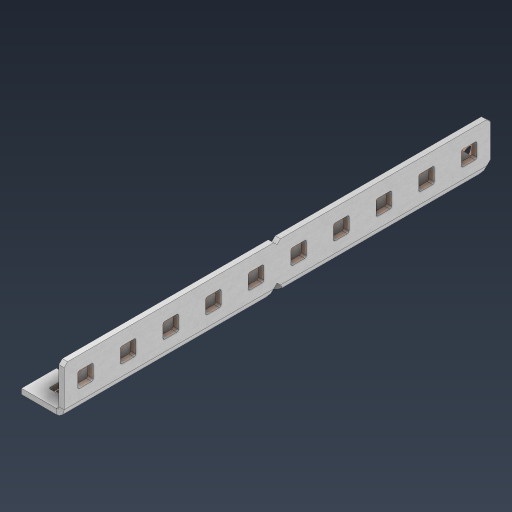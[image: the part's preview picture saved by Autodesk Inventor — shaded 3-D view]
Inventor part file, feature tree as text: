
AUTODESK INVENTOR PART (.ipt)
format: ipt  version: 2024.3 (Build 283343000, 343)  size: 601,600 bytes
history: native  units: in
note: dims shown in document units (in); Inventor stores cm internally (conversion verified against a paired STEP export)
features: other x37, extrude x28, sheet_metal_op x11, pattern_linear x2, mirror x1, chamfer x1, sketch x1
ambient origin geometry x8: Origin, YZ Plane, XZ Plane, XY Plane, X Axis, Y Axis, Z Axis, Center Point
bodies: Solid1 (feature_tree), Body (feature_tree)
feature tree (81):
  sheet_metal_op  "Flanges"
  other  "Flange Pattern Plane"
  other  "Flange Pattern Sketch"
  sheet_metal_op  "Flange Pattern"
  sheet_metal_op  "Body Pattern"
  pattern_linear  "Center Pattern"  Spacing1=5.0in  [1 undecoded]
  other  "Arc Length"
  mirror  "Notch Mirror"
  pattern_linear  "Notch Pattern"  Spacing1=0.0625in  [1 undecoded]
  chamfer  "End Chamfer"
  extrude  "Half Cut"  Depth=0.0625in
  other  "Plate1"
  sketch  "Sketch2"  dims[d0=1.0in d1=5.0in d2=0.0625in d3=0.0625in d4=0.0312in d5=0.125in d6=0.0625in d7=0.5in d8=90.0deg d9=0.0312in d10=0.25in d11=0.0625in d12=0.0625in d16=0.182in d17=0.02in d18=0.0625in d19=0.0in d20=0.25in d21=0.25in d38=3.937in d40=0.5in d41=0.3937in d43=1.0in d46=0.172in d47=1.0in d48=0.0in d49=0.182in d50=0.02in d51=0.25in d52=0.25in d53=0.0625in d54=0.0in d55=0.172in d56=1.0in d57=0.0in d58=0.25in d60=3.937in d62=0.5in d63=0.3937in d65=0.5in d85=0.1473in d86=0.1782in d88=0.04in d89=0.0625in d90=0.0in d91=0.04in d92=0.0491in d95=2.5in d96=0.04in d97=0.25in d98=45.0deg d99=0.25in d100=0.5in d101=0.0in d102=2.497in d106=0.182in d107=0.02in d108=0.5in d109=0.5in d110=0.0625in d111=0.0in d112=0.172in d113=0.5in d114=0.0in d117=0.5in d118=0.5in d119=0.5in]
  other  "Plate2"
  sheet_metal_op  "Bend1"
  sheet_metal_op  "Corner1"
  other  "Srf1"
  other  "Srf2"
  other  "Srf91"
  sheet_metal_op  "Body Pattern Sketch"
  other  "Srf92"
  other  "Srf786"
  other  "Srf823"
  other  "Srf824"
  other  "Srf825"
  other  "Srf826"
  other  "Srf827"
  other  "Srf828"
  other  "Srf829"
  other  "Srf856"
  other  "Srf857"
  other  "Srf858"
  other  "Srf859"
  other  "Srf860"
  other  "Srf861"
  other  "Srf862"
  other  "Srf889"
  other  "Srf890"
  other  "Srf891"
  other  "Srf892"
  other  "Srf893"
  other  "Srf894"
  other  "Srf895"
  other  "Srf896"
  other  "Srf922"
  other  "Srf959"
  other  "Srf996"
  sheet_metal_op  "Flange Stamp"
  sheet_metal_op  "Flange Circle"
  sheet_metal_op  "Body Stamp"
  sheet_metal_op  "Body Circle"
  other  "Center Stamp"
  other  "Center Circle"
  sheet_metal_op  "Notch"
  extrude  "ExtrusionSrf2"  Depth=0.5in
  extrude  "ExtrusionSrf92"  Depth=0.5in
  extrude  "ExtrusionSrf823"  Depth=0.0625in
  extrude  "ExtrusionSrf824"  Depth=0.5in TaperAngle=90.0deg
  extrude  "ExtrusionSrf825"  Depth=0.25in
  extrude  "ExtrusionSrf826"  Depth=0.0625in
  extrude  "ExtrusionSrf827"  Depth=0.0625in
  extrude  "ExtrusionSrf828"  Depth=0.182in
  extrude  "ExtrusionSrf829"  Depth=0.02in
  extrude  "ExtrusionSrf856"  Depth=0.0625in
  extrude  "ExtrusionSrf857"  TaperAngle=0.0deg  [1 undecoded]
  extrude  "ExtrusionSrf858"  Depth=0.25in
  extrude  "ExtrusionSrf859"  Depth=0.25in
  extrude  "ExtrusionSrf860"  Depth=0.5in
  extrude  "ExtrusionSrf861"  Depth=0.5in
  extrude  "ExtrusionSrf862"  Depth=1.0in TaperAngle=0.0deg
  extrude  "ExtrusionSrf889"  Depth=0.182in
  extrude  "ExtrusionSrf890"  Depth=0.02in
  extrude  "ExtrusionSrf891"  Depth=0.25in
  extrude  "ExtrusionSrf892"  Depth=0.25in
  extrude  "ExtrusionSrf893"  Depth=0.0625in
  extrude  "ExtrusionSrf894"  TaperAngle=0.0deg  [1 undecoded]
  extrude  "ExtrusionSrf895"  Depth=0.5in
  extrude  "ExtrusionSrf896"  Depth=1.0in TaperAngle=0.0deg
  extrude  "ExtrusionSrf922"  Depth=0.25in
  extrude  "ExtrusionSrf959"  Depth=0.5in
  extrude  "ExtrusionSrf996"  Depth=0.5in
note: 4 required parameter values undecoded (feature->parameter linkage not recoverable at this tier; creation-order binding heuristic only, values carry confidence <= 0.55)
